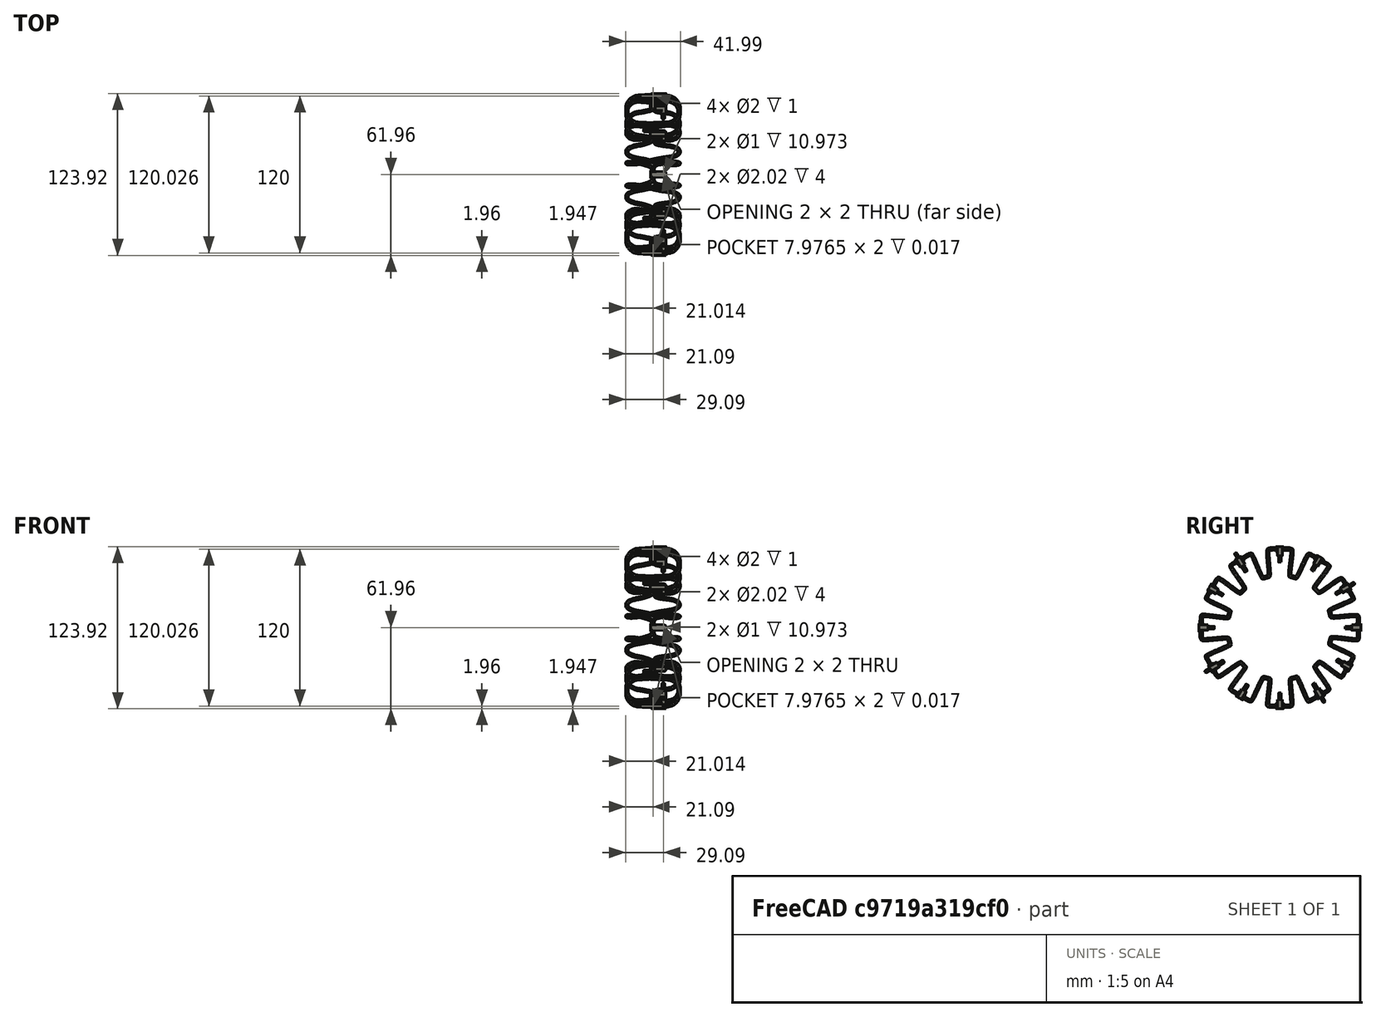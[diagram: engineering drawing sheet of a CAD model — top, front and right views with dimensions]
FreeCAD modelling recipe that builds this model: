
FCSTD DOCUMENT  (FreeCAD 0.19R24291 (Git))
Label: ring_vacuum_line01
License: All rights reserved
LicenseURL: http://en.wikipedia.org/wiki/All_rights_reserved
objects: Part::FeaturePython×8
note: 8 computed .brp shape members not serialized (recipe doc carries the construction recipe); baked Part::Feature solids carry a one-line shape summary decoded from their .brp

FEATURE [Part::FeaturePython] b_branch_pipe_tee01_001_  label="branch_pipe_tee01_001"  # a2plus imported part (geometry in sourceFile) (typed FeaturePython)
  Placement = pos=(8,0,-5) rot=(0,0,1;0rad)
  a2p_Version = V0.1
  fixedPosition = true
  objectType = a2pPart
  sourceFile = ./../cod/design CAD/branch_pipe_tee01.FCStd
  subassemblyImport = false
  timeLastImport = 1.64927e+09
  updateColors = true
FEATURE [Part::FeaturePython] b_vacuum_pip_ell04_001_  label="vacuum_pip_ell04_001"  # a2plus imported part (geometry in sourceFile) (typed FeaturePython)
  Placement = pos=(19.9058,-2.59288,-17.9638) rot=(-0.129428,0.129428,0.983106;1.58783rad)
  a2p_Version = V0.1
  fixedPosition = false
  objectType = a2pPart
  sourceFile = ./../cod/design CAD/vacuum_pip_ell04.FCStd
  subassemblyImport = false
  timeLastImport = 1.64882e+09
  updateColors = true
FEATURE [Part::FeaturePython] b_branch_pipe_tee01_001_001  label="branch_pipe_tee01_002"  # a2plus imported part (geometry in sourceFile) (typed FeaturePython)
  Placement = pos=(7.88457,27.3804,-12.0713) rot=(-1,0,0;0.523599rad)
  a2p_Version = V0.1
  fixedPosition = false
  objectType = a2pPart
  sourceFile = ./../cod/design CAD/branch_pipe_tee01.FCStd
  subassemblyImport = false
  timeLastImport = 1.64927e+09
  updateColors = true
FEATURE [Part::FeaturePython] b_branch_pipe_tee0_feeder01_001_  label="branch_pipe_tee0_feeder01_001"  # a2plus imported part (geometry in sourceFile) (typed FeaturePython)
  Placement = pos=(7.80143,47.1553,-31.7191) rot=(-1,0,0;1.0472rad)
  a2p_Version = V0.1
  fixedPosition = false
  objectType = a2pPart
  sourceFile = ./../cod/design CAD/branch_pipe_tee0_feeder01.FCStd
  subassemblyImport = false
  timeLastImport = 1.6508e+09
  updateColors = true
FEATURE [Part::FeaturePython] Array  # Draft array (typed FeaturePython)
  Angle = 360
  ArrayType = 1
  Axis = (1,0,0)
  Base = -> b_vacuum_pip_ell04_001_
  Center = (0,0,-60)
  Count = 12
  ExpandArray = false
  Fuse = true
  IntervalAxis = (0,0,0)
  IntervalX = (50,0,0)
  IntervalY = (0,50,0)
  IntervalZ = (0,0,50)
  NumberCircles = 3
  NumberPolar = 12
  NumberX = 2
  NumberY = 2
  NumberZ = 1
  PlacementList = 12 placements: [(19.9058,-2.59288,-17.9638),(19.9058,-23.2636,-24.892),(19.9058,-37.7009,-41.2274),(19.9058,-42.0362,-62.5929),(19.9058,-35.108,-83.2636),(19.9058,-18.7726,-97.7009),(19.9058,2.59288,-102.036),(19.9058,23.2636,-95.108),(19.9058,37.7009,-78.7726),(19.9058,42.0362,-57.4071),(19.9058,35.108,-36.7364),(19.9058,18.7726,-22.2991)]
  RadialDistance = 50
  ScaleList = (12) [(1,1,1),(1,1,1),(1,1,1),(1,1,1),(1,1,1),(1,1,1),(1,1,1),(1,1,1),(1,1,1),(1,1,1),(1,1,1),(1,1,1)]
  Symmetry = 1
  TangentialDistance = 25
FEATURE [Part::FeaturePython] Array001  # Draft array (typed FeaturePython)
  Angle = 360
  ArrayType = 1
  Axis = (1,0,0)
  Base = -> b_branch_pipe_tee01_001_
  Center = (0,0,-60)
  Count = 4
  ExpandArray = false
  Fuse = true
  IntervalAxis = (0,0,0)
  IntervalX = (50,0,0)
  IntervalY = (0,50,0)
  IntervalZ = (0,0,50)
  NumberCircles = 3
  NumberPolar = 4
  NumberX = 2
  NumberY = 2
  NumberZ = 1
  PlacementList = 4 placements: [(8,0,-5),(8,-55,-60),(8,-6.73556e-15,-115),(8,55,-60)]
  RadialDistance = 50
  ScaleList = (4) [(1,1,1),(1,1,1),(1,1,1),(1,1,1)]
  Symmetry = 1
  TangentialDistance = 25
FEATURE [Part::FeaturePython] Array002  # Draft array (typed FeaturePython)
  Angle = 360
  ArrayType = 1
  Axis = (1,0,0)
  Base = -> b_branch_pipe_tee01_001_001
  Center = (0,0,-60)
  Count = 4
  ExpandArray = false
  Fuse = true
  IntervalAxis = (0,0,0)
  IntervalX = (50,0,0)
  IntervalY = (0,50,0)
  IntervalZ = (0,0,50)
  NumberCircles = 3
  NumberPolar = 4
  NumberX = 2
  NumberY = 2
  NumberZ = 1
  PlacementList = 4 placements: [(7.88457,27.3804,-12.0713),(7.88457,-47.9287,-32.6196),(7.88457,-27.3804,-107.929),(7.88457,47.9287,-87.3804)]
  RadialDistance = 50
  ScaleList = (4) [(1,1,1),(1,1,1),(1,1,1),(1,1,1)]
  Symmetry = 1
  TangentialDistance = 25
FEATURE [Part::FeaturePython] Array003  # Draft array (typed FeaturePython)
  Angle = 360
  ArrayType = 1
  Axis = (1,0,0)
  Base = -> b_branch_pipe_tee0_feeder01_001_
  Center = (0,0,-60)
  Count = 4
  ExpandArray = false
  Fuse = true
  IntervalAxis = (0,0,0)
  IntervalX = (50,0,0)
  IntervalY = (0,50,0)
  IntervalZ = (0,0,50)
  NumberCircles = 3
  NumberPolar = 4
  NumberX = 2
  NumberY = 2
  NumberZ = 1
  PlacementList = 4 placements: [(7.80143,47.1553,-31.7191),(7.80143,-28.2809,-12.8447),(7.80143,-47.1553,-88.2809),(7.80143,28.2809,-107.155)]
  RadialDistance = 50
  ScaleList = (4) [(1,1,1),(1,1,1),(1,1,1),(1,1,1)]
  Symmetry = 1
  TangentialDistance = 25
